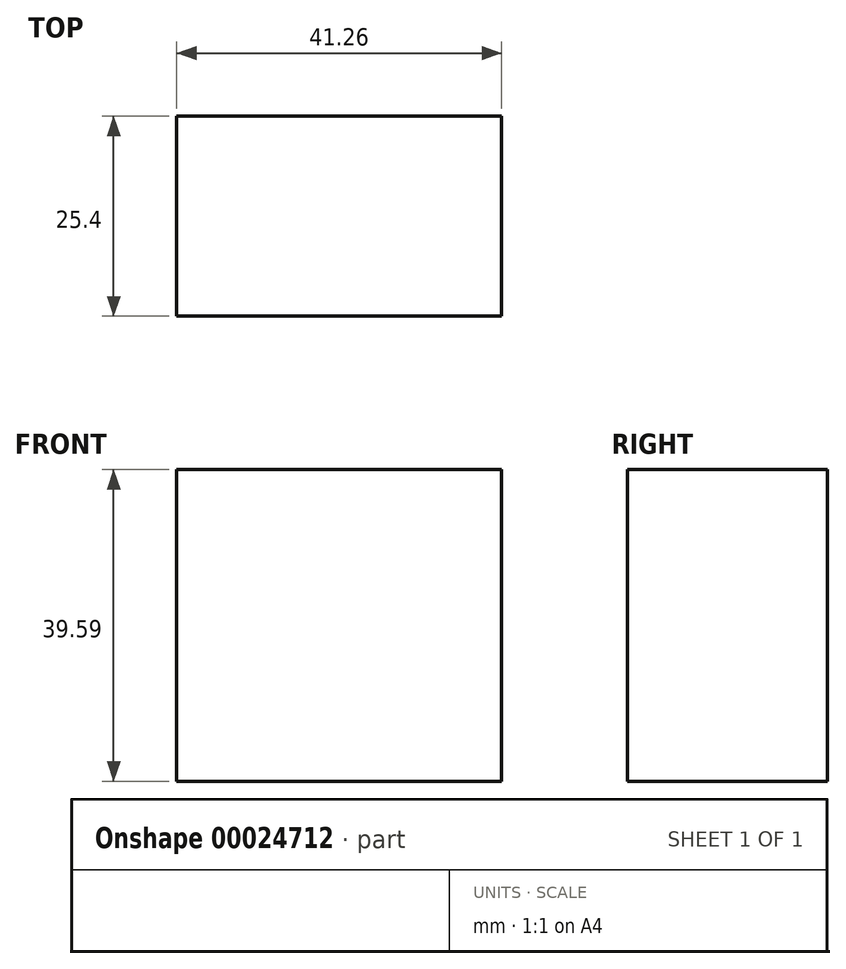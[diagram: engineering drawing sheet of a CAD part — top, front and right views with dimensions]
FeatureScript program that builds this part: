
annotation { "Feature Type Name" : "Feature", "Feature Type Description" : "" }
export const myFeature = defineFeature(function(context is Context, id is Id, definition is map)
    precondition{}
    {
        {
            var Q0;
            Q0=qCreatedBy(makeId("Front.planeOp"),FACE);
            var sketch = newSketch(context, id + "F0", { "sketchPlane" : qUnion([Q0])});
            skLineSegment(sketch, "E0.bottom", {"start": v(-55.02, 44.64) * mm, "end": v(-13.76, 44.64) * mm});
            skLineSegment(sketch, "E0.top", {"start": v(-55.02, 5.05) * mm, "end": v(-13.76, 5.05) * mm});
            skLineSegment(sketch, "E0.left", {"start": v(-55.02, 44.64) * mm, "end": v(-55.02, 5.05) * mm});
            skLineSegment(sketch, "E0.right", {"start": v(-13.76, 44.64) * mm, "end": v(-13.76, 5.05) * mm});
            skSolve(sketch);
        }
        {
            var Q0;
            Q0=makeQuery(id+"F0.imprint","IMPRINT",FACE,{"disambiguationData":[TD([[makeQuery(id+"F0.imprint","IMPRINT",EDGE,{"derivedFrom":sQuery(id+"F0.wireOp",EDGE,"E0.bottom")}),-1.0]])]});
            extrude(context, id + "F1", {"entities" : qUnion([Q0]), "depth" : 25.4 * mm});
        }
    });
